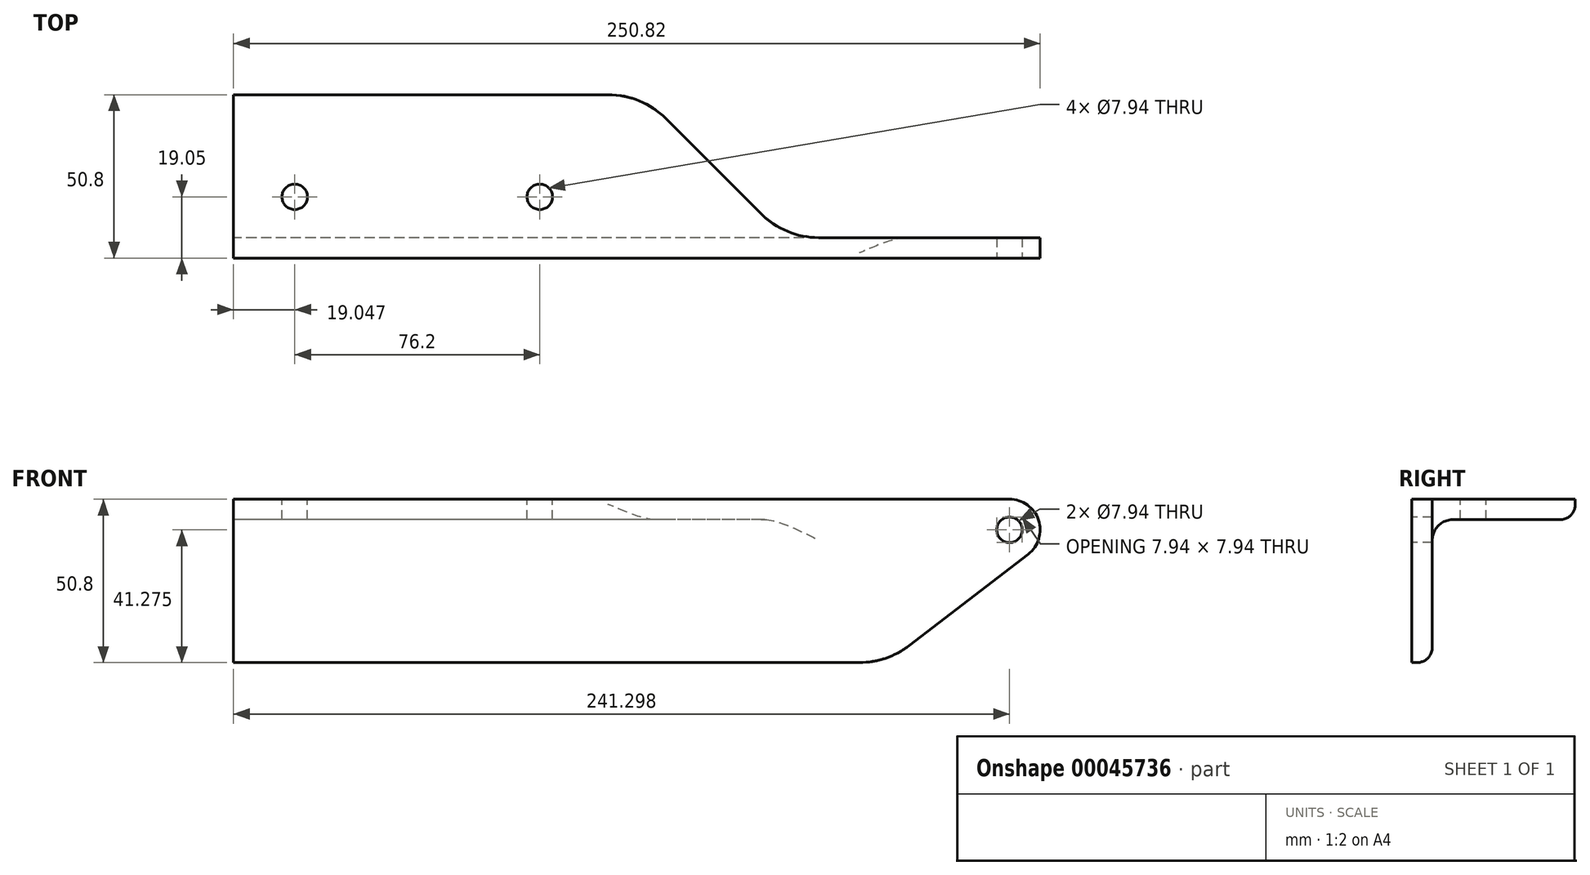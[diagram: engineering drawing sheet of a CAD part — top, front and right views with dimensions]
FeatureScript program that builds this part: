
annotation { "Feature Type Name" : "Feature", "Feature Type Description" : "" }
export const myFeature = defineFeature(function(context is Context, id is Id, definition is map)
    precondition{}
    {
        {
            var Q0;
            Q0=qCreatedBy(makeId("Right.planeOp"),FACE);
            var sketch = newSketch(context, id + "F0", { "sketchPlane" : qUnion([Q0])});
            skLineSegment(sketch, "E0", {"start": v(0, 0) * mm, "end": v(50.8, 0) * mm});
            skLineSegment(sketch, "E1", {"start": v(0, 0) * mm, "end": v(0, -50.8) * mm});
            skLineSegment(sketch, "E2.0", {"start": v(12.7, -6.35) * mm, "end": v(46.04, -6.35) * mm});
            skLineSegment(sketch, "E2.1", {"start": v(6.35, -12.7) * mm, "end": v(6.35, -46.04) * mm});
            skPoint(sketch, "E3.visualSharp", {"position": v(6.35, -6.35) * mm});
            skArc(sketch, "E3.filletArc", {"start": v(12.7, -6.35) * mm, "mid": v(8.2, -8.2) * mm, "end": v(6.35, -12.7) * mm});
            skLineSegment(sketch, "E4", {"start": v(1.59, -50.8) * mm, "end": v(0, -50.8) * mm});
            skLineSegment(sketch, "E5", {"start": v(50.8, -1.59) * mm, "end": v(50.8, 0) * mm});
            skPoint(sketch, "E6.visualSharp", {"position": v(50.8, -6.35) * mm});
            skArc(sketch, "E6.filletArc", {"start": v(46.04, -6.35) * mm, "mid": v(49.4, -4.96) * mm, "end": v(50.8, -1.59) * mm});
            skPoint(sketch, "E7.visualSharp", {"position": v(6.35, -50.8) * mm});
            skArc(sketch, "E7.filletArc", {"start": v(1.59, -50.8) * mm, "mid": v(4.96, -49.4) * mm, "end": v(6.35, -46.04) * mm});
            skSolve(sketch);
        }
        {
            var Q0;
            Q0=qSketchRegion(id+"F0",true);
            extrude(context, id + "F1", {"entities" : qUnion([Q0]), "endBound" : BoundingType.SYMMETRIC, "depth" : 250.82 * mm});
        }
        {
            var Q0;
            Q0=makeQuery(id+"F1.opExtrude","SWEPT_FACE",FACE,{"disambiguationData":[OSD([sQuery(id+"F0.wireOp",EDGE,"E0")])]});
            var sketch = newSketch(context, id + "F2", { "sketchPlane" : qUnion([Q0])});
            skLineSegment(sketch, "E8.0", {"start": v(125.41, 0) * mm, "end": v(-125.41, 0) * mm, "construction": true});
            skLineSegment(sketch, "E9.0", {"start": v(125.41, 19.05) * mm, "end": v(-125.41, 19.05) * mm, "construction": true});
            skLineSegment(sketch, "E10.0", {"start": v(-125.41, 0) * mm, "end": v(-125.41, 50.8) * mm, "construction": true});
            skLineSegment(sketch, "E11.0", {"start": v(-106.36, 0) * mm, "end": v(-106.36, 50.8) * mm, "construction": true});
            skLineSegment(sketch, "E12.0", {"start": v(-30.16, 0) * mm, "end": v(-30.16, 50.8) * mm, "construction": true});
            skPoint(sketch, "E13", {"position": v(-106.36, 19.05) * mm});
            skPoint(sketch, "E14", {"position": v(-30.16, 19.05) * mm});
            skSolve(sketch);
        }
        {
            var Q0;
            Q0=sQuery(id+"F2.wireOp",VERTEX,"E13");
            var Q1;
            Q1=sQuery(id+"F2.wireOp",VERTEX,"E14");
            var Q2;
            Q2=makeQuery(id+"F1.opExtrude","SWEPT_BODY",BODY,{"disambiguationData":[OSD([sQuery(id+"F0.wireOp",EDGE,"E0"),sQuery(id+"F0.wireOp",EDGE,"E1"),sQuery(id+"F0.wireOp",EDGE,"E2.0"),sQuery(id+"F0.wireOp",EDGE,"E2.1"),sQuery(id+"F0.wireOp",EDGE,"E3.filletArc"),sQuery(id+"F0.wireOp",EDGE,"E4"),sQuery(id+"F0.wireOp",EDGE,"E5"),sQuery(id+"F0.wireOp",EDGE,"E6.filletArc"),sQuery(id+"F0.wireOp",EDGE,"E7.filletArc")])]});
            hole(context, id + "F3", {"style" : HoleStyle.SIMPLE, "holeDiameter" : 7.94 * mm, "endStyle" : HoleEndStyle.THROUGH, "locations" : qUnion([Q0, Q1]), "scope" : qUnion([Q2])});
        }
        {
            var Q0;
            Q0=makeQuery(id+"F1.opExtrude","SWEPT_FACE",FACE,{"disambiguationData":[OSD([sQuery(id+"F0.wireOp",EDGE,"E0")])]});
            var sketch = newSketch(context, id + "F4", { "sketchPlane" : qUnion([Q0])});
            skLineSegment(sketch, "E15.0", {"start": v(125.41, 6.35) * mm, "end": v(46.04, 6.35) * mm});
            skLineSegment(sketch, "E16.0", {"start": v(-125.41, 0) * mm, "end": v(-125.41, 50.8) * mm, "construction": true});
            skLineSegment(sketch, "E17.0", {"start": v(1.59, 0) * mm, "end": v(1.59, 50.8) * mm, "construction": true});
            skLineSegment(sketch, "E18.0", {"start": v(46.04, 0) * mm, "end": v(46.04, 50.8) * mm, "construction": true});
            skLineSegment(sketch, "E19", {"start": v(46.04, 6.35) * mm, "end": v(1.59, 50.8) * mm});
            skLineSegment(sketch, "E20", {"start": v(1.59, 50.8) * mm, "end": v(125.41, 50.8) * mm});
            skLineSegment(sketch, "E21", {"start": v(125.41, 50.8) * mm, "end": v(125.41, 6.35) * mm});
            skPoint(sketch, "E22.orphan", {"position": v(-125.41, 6.35) * mm});
            skSolve(sketch);
        }
        {
            var Q0;
            Q0=qSketchRegion(id+"F4",true);
            extrude(context, id + "F5", {"entities" : qUnion([Q0]), "operationType" : NewBodyOperationType.REMOVE, "endBound" : BoundingType.THROUGH_ALL, "oppositeDirection" : true, "depth" : 25.4 * mm});
        }
        {
            var Q0;
            Q0=makeQuery(id+"F1.opExtrude","SWEPT_FACE",FACE,{"disambiguationData":[OSD([sQuery(id+"F0.wireOp",EDGE,"E0")])]});
            var sketch = newSketch(context, id + "F6", { "sketchPlane" : qUnion([Q0])});
            skLineSegment(sketch, "E23.0", {"start": v(-8.93, 50.8) * mm, "end": v(-125.41, 50.8) * mm});
            skLineSegment(sketch, "E24.0", {"start": v(46.04, 6.35) * mm, "end": v(9.03, 43.36) * mm});
            skLineSegment(sketch, "E25.rect.bottom", {"start": v(-21.33, 63.74) * mm, "end": v(24.5, 63.74) * mm});
            skLineSegment(sketch, "E25.rect.top", {"start": v(14.53, 37.86) * mm, "end": v(24.5, 37.86) * mm});
            skLineSegment(sketch, "E25.rect.left", {"start": v(-21.33, 63.74) * mm, "end": v(-21.33, 50.8) * mm});
            skLineSegment(sketch, "E25.rect.right", {"start": v(24.5, 63.74) * mm, "end": v(24.5, 37.86) * mm});
            skPoint(sketch, "E25.rect.middle", {"position": v(1.59, 50.8) * mm});
            skArc(sketch, "E26.filletArc", {"start": v(9.03, 43.36) * mm, "mid": v(0.79, 48.87) * mm, "end": v(-8.93, 50.8) * mm});
            skPoint(sketch, "E27.orphan", {"position": v(-21.33, 37.86) * mm});
            skSolve(sketch);
        }
        {
            var Q0;
            Q0=qSketchRegion(id+"F6",true);
            extrude(context, id + "F7", {"entities" : qUnion([Q0]), "operationType" : NewBodyOperationType.REMOVE, "endBound" : BoundingType.THROUGH_ALL, "oppositeDirection" : true, "depth" : 25.4 * mm});
        }
        {
            var Q0;
            Q0=makeQuery(id+"F5.boolean.opBoolean","COPY",EDGE,{"derivedFrom":makeQuery(id+"F5.opExtrude","SWEPT_EDGE",EDGE,{"disambiguationData":[OSD([sQuery(id+"F4.wireOp",EDGE,"E15.0"),sQuery(id+"F4.wireOp",EDGE,"E19")])]})});
            fillet(context, id + "F8", {"entities" : qUnion([Q0]), "radius" : 25.4 * mm, "tangentPropagation" : true, "allowEdgeOverflow" : false});
        }
        {
            var Q0;
            Q0=makeQuery(id+"F1.opExtrude","SWEPT_FACE",FACE,{"disambiguationData":[OSD([sQuery(id+"F0.wireOp",EDGE,"E1")])]});
            var sketch = newSketch(context, id + "F9", { "sketchPlane" : qUnion([Q0])});
            skLineSegment(sketch, "E28.0", {"start": v(-125.41, 0) * mm, "end": v(-125.41, -50.8) * mm, "construction": true});
            skLineSegment(sketch, "E29.0", {"start": v(115.89, 0) * mm, "end": v(115.89, -50.8) * mm, "construction": true});
            skLineSegment(sketch, "E30.0", {"start": v(125.41, -9.53) * mm, "end": v(-125.41, -9.53) * mm, "construction": true});
            skArc(sketch, "E31", {"start": v(115.89, -19.05) * mm, "mid": v(125.41, -9.53) * mm, "end": v(115.89, 0) * mm});
            skLineSegment(sketch, "E32.0", {"start": v(77.79, 0) * mm, "end": v(77.79, -50.8) * mm});
            skLineSegment(sketch, "E33.0", {"start": v(125.41, -50.8) * mm, "end": v(-125.41, -50.8) * mm});
            skLineSegment(sketch, "E34", {"start": v(77.79, -50.8) * mm, "end": v(121.69, -17.08) * mm});
            skLineSegment(sketch, "E35", {"start": v(115.89, 0) * mm, "end": v(115.89, 14.21) * mm});
            skLineSegment(sketch, "E36", {"start": v(115.89, 14.21) * mm, "end": v(141.57, 14.21) * mm});
            skLineSegment(sketch, "E37", {"start": v(141.57, 14.21) * mm, "end": v(141.57, -61.2) * mm});
            skLineSegment(sketch, "E38", {"start": v(141.57, -61.2) * mm, "end": v(77.79, -61.2) * mm});
            skLineSegment(sketch, "E39", {"start": v(77.79, -61.2) * mm, "end": v(77.79, -50.8) * mm});
            skSolve(sketch);
        }
        {
            var Q0;
            Q0=qSketchRegion(id+"F9",true);
            extrude(context, id + "F10", {"entities" : qUnion([Q0]), "operationType" : NewBodyOperationType.REMOVE, "endBound" : BoundingType.THROUGH_ALL, "oppositeDirection" : true, "depth" : 25.4 * mm});
        }
        {
            var Q0;
            {var subQ2=sQuery(id+"F9.wireOp",EDGE,"E32.0");Q0=makeQuery(id+"F9.imprint","IMPRINT",FACE,{"disambiguationData":[TD([[makeQuery(id+"F9.imprint","IMPRINT",EDGE,{"derivedFrom":subQ2}),1.0]])]});}
            var sketch = newSketch(context, id + "F11", { "sketchPlane" : qUnion([Q0])});
            skLineSegment(sketch, "E40.0", {"start": v(125.41, -9.53) * mm, "end": v(-125.41, -9.53) * mm, "construction": true});
            skLineSegment(sketch, "E41.0", {"start": v(115.89, 0) * mm, "end": v(115.89, -50.8) * mm, "construction": true});
            skPoint(sketch, "E42", {"position": v(115.89, -9.53) * mm});
            skSolve(sketch);
        }
        {
            var Q0;
            Q0=sQuery(id+"F11.wireOp",VERTEX,"E42");
            var Q1;
            Q1=makeQuery(id+"F1.opExtrude","SWEPT_BODY",BODY,{"disambiguationData":[OSD([sQuery(id+"F0.wireOp",EDGE,"E0"),sQuery(id+"F0.wireOp",EDGE,"E1"),sQuery(id+"F0.wireOp",EDGE,"E2.0"),sQuery(id+"F0.wireOp",EDGE,"E2.1"),sQuery(id+"F0.wireOp",EDGE,"E3.filletArc"),sQuery(id+"F0.wireOp",EDGE,"E4"),sQuery(id+"F0.wireOp",EDGE,"E5"),sQuery(id+"F0.wireOp",EDGE,"E6.filletArc"),sQuery(id+"F0.wireOp",EDGE,"E7.filletArc")])]});
            hole(context, id + "F12", {"style" : HoleStyle.SIMPLE, "holeDiameter" : 7.94 * mm, "endStyle" : HoleEndStyle.THROUGH, "locations" : qUnion([Q0]), "scope" : qUnion([Q1])});
        }
        {
            var Q0;
            Q0=makeQuery(id+"F1.opExtrude","SWEPT_FACE",FACE,{"disambiguationData":[OSD([sQuery(id+"F0.wireOp",EDGE,"E1")])]});
            var sketch = newSketch(context, id + "F13", { "sketchPlane" : qUnion([Q0])});
            skLineSegment(sketch, "E43.0", {"start": v(84.63, -45.54) * mm, "end": v(92.94, -39.16) * mm});
            skLineSegment(sketch, "E44.0", {"start": v(69.16, -50.8) * mm, "end": v(57.52, -50.8) * mm});
            skPoint(sketch, "E45.visualSharp", {"position": v(77.79, -50.8) * mm});
            skArc(sketch, "E45.filletArc", {"start": v(69.16, -50.8) * mm, "mid": v(77.33, -49.45) * mm, "end": v(84.63, -45.54) * mm});
            skLineSegment(sketch, "E46.rect.bottom", {"start": v(92.94, -39.16) * mm, "end": v(98.06, -39.16) * mm});
            skLineSegment(sketch, "E46.rect.top", {"start": v(57.52, -62.44) * mm, "end": v(98.06, -62.44) * mm});
            skLineSegment(sketch, "E46.rect.left", {"start": v(57.52, -50.8) * mm, "end": v(57.52, -62.44) * mm});
            skLineSegment(sketch, "E46.rect.right", {"start": v(98.06, -39.16) * mm, "end": v(98.06, -62.44) * mm});
            skPoint(sketch, "E47.orphan", {"position": v(57.52, -39.16) * mm});
            skPoint(sketch, "E48.orphan", {"position": v(-125.41, -50.8) * mm});
            skPoint(sketch, "E49.orphan", {"position": v(121.69, -17.08) * mm});
            skSolve(sketch);
        }
        {
            var Q0;
            Q0=qSketchRegion(id+"F13",true);
            extrude(context, id + "F14", {"entities" : qUnion([Q0]), "operationType" : NewBodyOperationType.REMOVE, "endBound" : BoundingType.THROUGH_ALL, "oppositeDirection" : true, "depth" : 25.4 * mm});
        }
    });
